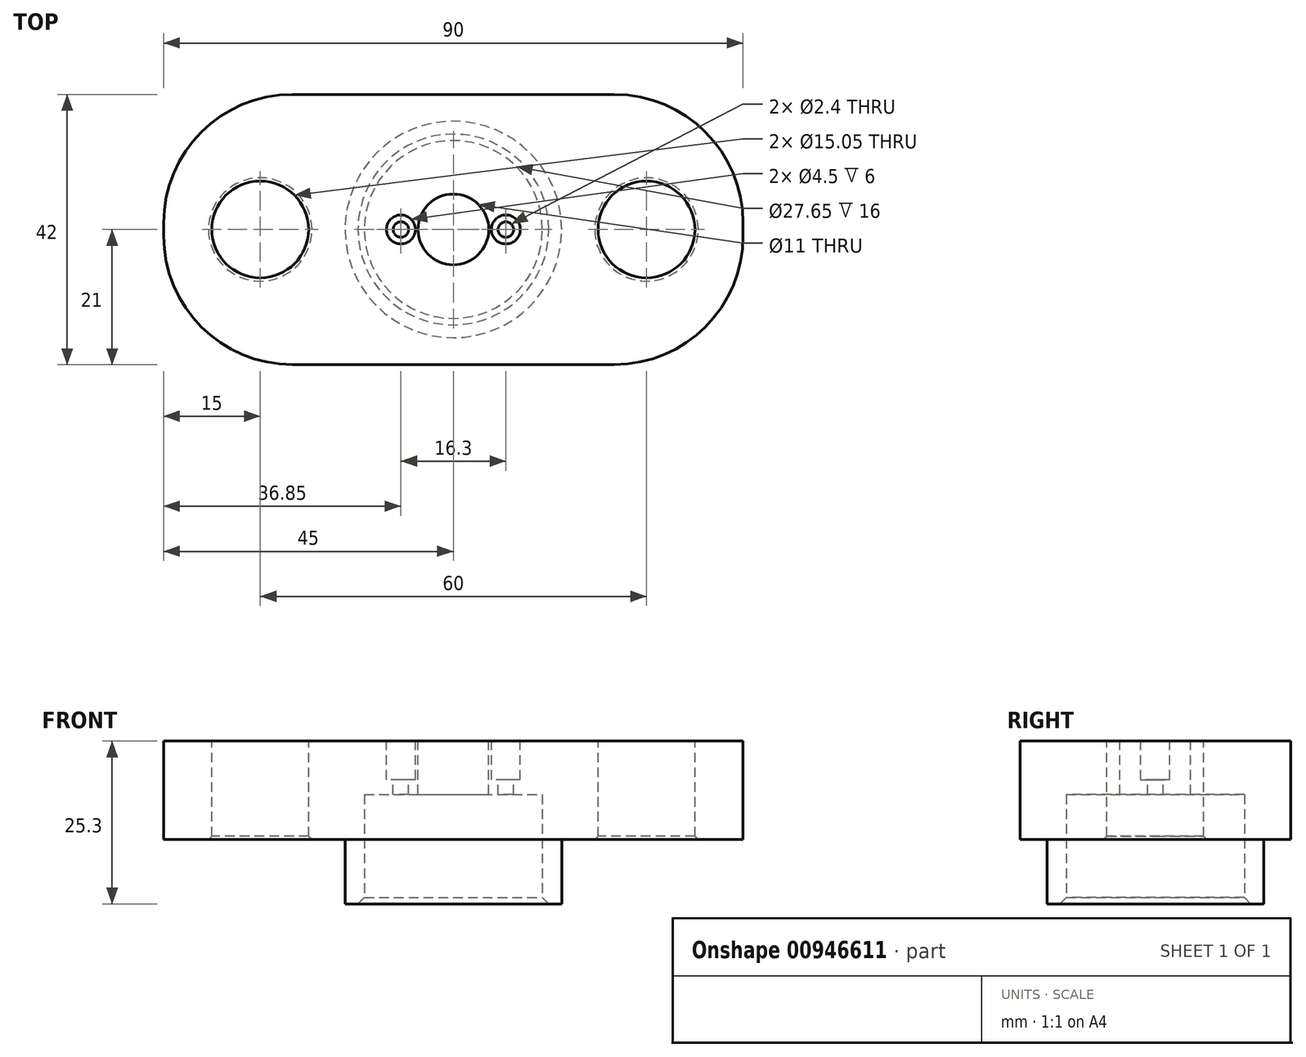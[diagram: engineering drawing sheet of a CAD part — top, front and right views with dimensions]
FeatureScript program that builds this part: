
annotation { "Feature Type Name" : "Feature", "Feature Type Description" : "" }
export const myFeature = defineFeature(function(context is Context, id is Id, definition is map)
    precondition{}
    {
        {
            var Q0;
            Q0=qCreatedBy(makeId("Top.planeOp"),FACE);
            var sketch = newSketch(context, id + "F0", { "sketchPlane" : qUnion([Q0])});
            skLineSegment(sketch, "E0.bottom", {"start": v(-45, 21) * mm, "end": v(45, 21) * mm});
            skLineSegment(sketch, "E0.top", {"start": v(-45, -21) * mm, "end": v(45, -21) * mm});
            skLineSegment(sketch, "E0.left", {"start": v(-45, 21) * mm, "end": v(-45, -21) * mm});
            skLineSegment(sketch, "E0.right", {"start": v(45, 21) * mm, "end": v(45, -21) * mm});
            skSolve(sketch);
        }
        {
            var Q0;
            Q0 = qSketchRegion(id + "F0", true);
            extrude(context, id + "F1", {"entities" : qUnion([Q0]), "depth" : 15.3 * mm, "offsetDistance" : 25 * mm});
        }
        {
            var Q0;
            Q0=makeQuery(id+"F1.opExtrude","SWEPT_EDGE",EDGE,{"disambiguationData":[OSD([sQuery(id+"F0.wireOp",EDGE,"E0.top"),sQuery(id+"F0.wireOp",EDGE,"E0.left")])]});
            var Q1;
            Q1=makeQuery(id+"F1.opExtrude","SWEPT_EDGE",EDGE,{"disambiguationData":[OSD([sQuery(id+"F0.wireOp",EDGE,"E0.bottom"),sQuery(id+"F0.wireOp",EDGE,"E0.left")])]});
            fillet(context, id + "F2", {"entities" : qUnion([Q0, Q1]), "radius" : 20 * mm, "tangentPropagation" : true, "allowEdgeOverflow" : false});
        }
        {
            var Q0;
            Q0=makeQuery(id+"F1.opExtrude","SWEPT_EDGE",EDGE,{"disambiguationData":[OSD([sQuery(id+"F0.wireOp",EDGE,"E0.bottom"),sQuery(id+"F0.wireOp",EDGE,"E0.right")])]});
            var Q1;
            Q1=makeQuery(id+"F1.opExtrude","SWEPT_EDGE",EDGE,{"disambiguationData":[OSD([sQuery(id+"F0.wireOp",EDGE,"E0.top"),sQuery(id+"F0.wireOp",EDGE,"E0.right")])]});
            fillet(context, id + "F3", {"entities" : qUnion([Q0, Q1]), "radius" : 20 * mm, "tangentPropagation" : true, "allowEdgeOverflow" : false});
        }
        {
            var Q0;
            Q0=makeQuery(id+"F1.opExtrude","CAP_FACE",FACE,{"disambiguationData":[OSD([sQuery(id+"F0.wireOp",EDGE,"E0.bottom"),sQuery(id+"F0.wireOp",EDGE,"E0.top"),sQuery(id+"F0.wireOp",EDGE,"E0.left"),sQuery(id+"F0.wireOp",EDGE,"E0.right")])],"isStart":true});
            var sketch = newSketch(context, id + "F4", { "sketchPlane" : qUnion([Q0])});
            skCircle(sketch, "E1", {"center": v(0, 0) * mm, "radius": 13.82 * mm});
            skSolve(sketch);
        }
        {
            var Q0;
            Q0 = qSketchRegion(id + "F4", true);
            extrude(context, id + "F5", {"entities" : qUnion([Q0]), "operationType" : NewBodyOperationType.REMOVE, "oppositeDirection" : true, "depth" : 7 * mm, "offsetDistance" : 25 * mm});
        }
        {
            var Q0;
            Q0=makeQuery(id+"F1.opExtrude","CAP_FACE",FACE,{"disambiguationData":[OSD([sQuery(id+"F0.wireOp",EDGE,"E0.bottom"),sQuery(id+"F0.wireOp",EDGE,"E0.top"),sQuery(id+"F0.wireOp",EDGE,"E0.left"),sQuery(id+"F0.wireOp",EDGE,"E0.right")])],"isStart":false});
            var sketch = newSketch(context, id + "F6", { "sketchPlane" : qUnion([Q0])});
            skCircle(sketch, "E2", {"center": v(0, 0) * mm, "radius": 5.5 * mm});
            skSolve(sketch);
        }
        {
            var Q0;
            Q0 = qSketchRegion(id + "F6", true);
            extrude(context, id + "F7", {"entities" : qUnion([Q0]), "operationType" : NewBodyOperationType.REMOVE, "oppositeDirection" : true, "depth" : 10 * mm, "offsetDistance" : 25 * mm});
        }
        {
            var Q0;
            Q0=makeQuery(id+"F1.opExtrude","CAP_FACE",FACE,{"disambiguationData":[OSD([sQuery(id+"F0.wireOp",EDGE,"E0.bottom"),sQuery(id+"F0.wireOp",EDGE,"E0.top"),sQuery(id+"F0.wireOp",EDGE,"E0.left"),sQuery(id+"F0.wireOp",EDGE,"E0.right")])],"isStart":false});
            var sketch = newSketch(context, id + "F8", { "sketchPlane" : qUnion([Q0])});
            skCircle(sketch, "E3", {"center": v(-30, 0) * mm, "radius": 7.53 * mm});
            skCircle(sketch, "E4", {"center": v(30, 0) * mm, "radius": 7.53 * mm});
            skCircle(sketch, "E5", {"center": v(-8.15, 0) * mm, "radius": 1.2 * mm});
            skCircle(sketch, "E6", {"center": v(8.15, 0) * mm, "radius": 1.2 * mm});
            skSolve(sketch);
        }
        {
            var Q0;
            Q0 = qSketchRegion(id + "F8", true);
            extrude(context, id + "F9", {"entities" : qUnion([Q0]), "operationType" : NewBodyOperationType.REMOVE, "oppositeDirection" : true, "depth" : 18 * mm, "offsetDistance" : 25 * mm});
        }
        {
            var Q0;
            Q0=makeQuery(id+"F1.opExtrude","CAP_FACE",FACE,{"disambiguationData":[OSD([sQuery(id+"F0.wireOp",EDGE,"E0.bottom"),sQuery(id+"F0.wireOp",EDGE,"E0.top"),sQuery(id+"F0.wireOp",EDGE,"E0.left"),sQuery(id+"F0.wireOp",EDGE,"E0.right")])],"isStart":true});
            var sketch = newSketch(context, id + "F10", { "sketchPlane" : qUnion([Q0])});
            skCircle(sketch, "E7", {"center": v(0, 0) * mm, "radius": 16.82 * mm});
            skSolve(sketch);
        }
        {
            var Q0;
            Q0=makeQuery(id+"F10.imprint","IMPRINT",FACE,{"disambiguationData":[TD([[makeQuery(id+"F10.imprint","IMPRINT",EDGE,{"derivedFrom":sQuery(id+"F10.wireOp",EDGE,"E7")}),1.0]])]});
            extrude(context, id + "F11", {"entities" : qUnion([Q0]), "operationType" : NewBodyOperationType.ADD, "depth" : 10 * mm, "offsetDistance" : 25 * mm});
        }
        {
            var Q0;
            Q0=makeQuery(id+"F11.opExtrude","CAP_EDGE",EDGE,{"disambiguationData":[OSD([sQuery(id+"F4.wireOp",EDGE,"E1")])],"isStart":false});
            chamfer(context, id + "F12", {"entities" : qUnion([Q0]), "width" : 1 * mm, "tangentPropagation" : true});
        }
        {
            var Q0;
            Q0=makeQuery(id+"F9.boolean.opBoolean","INTERSECT",EDGE,{"derivedFrom":[makeQuery(id+"F1.opExtrude","CAP_FACE",FACE,{"disambiguationData":[OSD([sQuery(id+"F0.wireOp",EDGE,"E0.bottom"),sQuery(id+"F0.wireOp",EDGE,"E0.top"),sQuery(id+"F0.wireOp",EDGE,"E0.left"),sQuery(id+"F0.wireOp",EDGE,"E0.right")])],"isStart":true}),makeQuery(id+"F9.opExtrude","SWEPT_FACE",FACE,{"disambiguationData":[OSD([sQuery(id+"F8.wireOp",EDGE,"E3")])]})]});
            var Q1;
            Q1=makeQuery(id+"F9.boolean.opBoolean","INTERSECT",EDGE,{"derivedFrom":[makeQuery(id+"F1.opExtrude","CAP_FACE",FACE,{"disambiguationData":[OSD([sQuery(id+"F0.wireOp",EDGE,"E0.bottom"),sQuery(id+"F0.wireOp",EDGE,"E0.top"),sQuery(id+"F0.wireOp",EDGE,"E0.left"),sQuery(id+"F0.wireOp",EDGE,"E0.right")])],"isStart":true}),makeQuery(id+"F9.opExtrude","SWEPT_FACE",FACE,{"disambiguationData":[OSD([sQuery(id+"F8.wireOp",EDGE,"E4")])]})]});
            chamfer(context, id + "F13", {"entities" : qUnion([Q0, Q1]), "width" : .5 * mm, "tangentPropagation" : true});
        }
        {
            var Q0;
            Q0=makeQuery(id+"F1.opExtrude","CAP_FACE",FACE,{"disambiguationData":[OSD([sQuery(id+"F0.wireOp",EDGE,"E0.bottom"),sQuery(id+"F0.wireOp",EDGE,"E0.top"),sQuery(id+"F0.wireOp",EDGE,"E0.left"),sQuery(id+"F0.wireOp",EDGE,"E0.right")])],"isStart":false});
            var sketch = newSketch(context, id + "F14", { "sketchPlane" : qUnion([Q0])});
            skCircle(sketch, "E8", {"center": v(-8.15, 0) * mm, "radius": 2.25 * mm});
            skCircle(sketch, "E9", {"center": v(8.15, 0) * mm, "radius": 2.25 * mm});
            skSolve(sketch);
        }
        {
            var Q0;
            Q0 = qSketchRegion(id + "F14", true);
            extrude(context, id + "F15", {"entities" : qUnion([Q0]), "operationType" : NewBodyOperationType.REMOVE, "oppositeDirection" : true, "depth" : 6 * mm, "offsetDistance" : 25 * mm});
        }
    });
